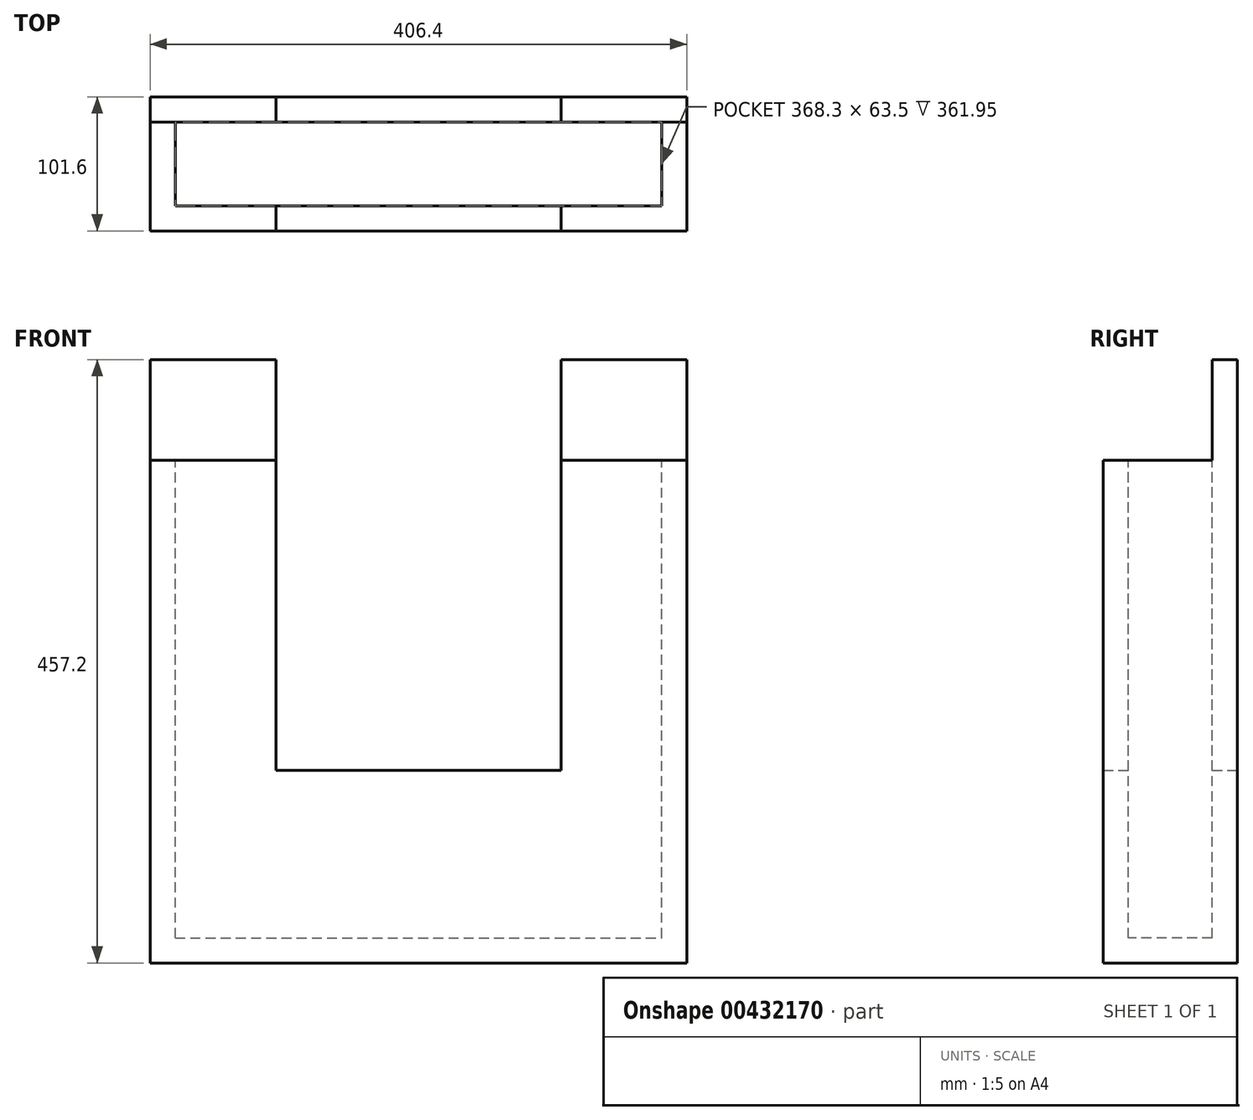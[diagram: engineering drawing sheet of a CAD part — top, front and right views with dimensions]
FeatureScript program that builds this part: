
annotation { "Feature Type Name" : "Feature", "Feature Type Description" : "" }
export const myFeature = defineFeature(function(context is Context, id is Id, definition is map)
    precondition{}
    {
        {
            var Q0;
            Q0=qCreatedBy(makeId("Front.planeOp"),FACE);
            var sketch = newSketch(context, id + "F0", { "sketchPlane" : qUnion([Q0])});
            skLineSegment(sketch, "E0.bottom", {"start": v(-199.76, 190.43) * mm, "end": v(206.64, 190.43) * mm});
            skLineSegment(sketch, "E0.top", {"start": v(-199.76, -266.77) * mm, "end": v(206.64, -266.77) * mm});
            skLineSegment(sketch, "E0.left", {"start": v(-199.76, 190.43) * mm, "end": v(-199.76, -266.77) * mm});
            skLineSegment(sketch, "E0.right", {"start": v(206.64, 190.43) * mm, "end": v(206.64, -266.77) * mm});
            skSolve(sketch);
        }
        {
            var Q0;
            Q0 = qSketchRegion(id + "F0", true);
            extrude(context, id + "F1", {"entities" : qUnion([Q0]), "depth" : 101.6 * mm});
        }
        {
            var Q0;
            Q0=makeQuery(id+"F1.opExtrude","SWEPT_FACE",FACE,{"disambiguationData":[OSD([sQuery(id+"F0.wireOp",EDGE,"E0.right")])]});
            var sketch = newSketch(context, id + "F2", { "sketchPlane" : qUnion([Q0])});
            skLineSegment(sketch, "E1.bottom", {"start": v(-101.6, 190.43) * mm, "end": v(-19.05, 190.43) * mm});
            skLineSegment(sketch, "E1.top", {"start": v(-101.6, 114.23) * mm, "end": v(-19.05, 114.23) * mm});
            skLineSegment(sketch, "E1.left", {"start": v(-101.6, 190.43) * mm, "end": v(-101.6, 114.23) * mm});
            skLineSegment(sketch, "E1.right", {"start": v(-19.05, 190.43) * mm, "end": v(-19.05, 114.23) * mm});
            skSolve(sketch);
        }
        {
            var Q0;
            Q0=makeQuery(id+"F2.imprint","IMPRINT",FACE,{"disambiguationData":[TD([[makeQuery(id+"F2.imprint","IMPRINT",EDGE,{"derivedFrom":sQuery(id+"F2.wireOp",EDGE,"E1.bottom")}),-1.0]])]});
            extrude(context, id + "F3", {"entities" : qUnion([Q0]), "operationType" : NewBodyOperationType.REMOVE, "oppositeDirection" : true, "depth" : 406.4 * mm});
        }
        {
            var Q0;
            Q0=makeQuery(id+"F3.boolean.opBoolean","COPY",FACE,{"derivedFrom":makeQuery(id+"F3.opExtrude","SWEPT_FACE",FACE,{"disambiguationData":[OSD([sQuery(id+"F2.wireOp",EDGE,"E1.top")])]})});
            var sketch = newSketch(context, id + "F4", { "sketchPlane" : qUnion([Q0])});
            skLineSegment(sketch, "E2.bottom", {"start": v(-180.7, -19.05) * mm, "end": v(187.6, -19.05) * mm});
            skLineSegment(sketch, "E2.top", {"start": v(-180.7, -82.55) * mm, "end": v(187.6, -82.55) * mm});
            skLineSegment(sketch, "E2.left", {"start": v(-180.7, -19.05) * mm, "end": v(-180.7, -82.55) * mm});
            skLineSegment(sketch, "E2.right", {"start": v(187.6, -19.05) * mm, "end": v(187.6, -82.55) * mm});
            skSolve(sketch);
        }
        {
            var Q0;
            Q0=makeQuery(id+"F4.imprint","IMPRINT",FACE,{"disambiguationData":[TD([[makeQuery(id+"F4.imprint","IMPRINT",EDGE,{"derivedFrom":sQuery(id+"F4.wireOp",EDGE,"E2.bottom")}),-1.0]])]});
            extrude(context, id + "F5", {"entities" : qUnion([Q0]), "operationType" : NewBodyOperationType.REMOVE, "oppositeDirection" : true, "depth" : 361.95 * mm});
        }
        {
            var Q0;
            Q0=makeQuery(id+"F1.opExtrude","CAP_FACE",FACE,{"disambiguationData":[OSD([sQuery(id+"F0.wireOp",EDGE,"E0.bottom"),sQuery(id+"F0.wireOp",EDGE,"E0.top"),sQuery(id+"F0.wireOp",EDGE,"E0.left"),sQuery(id+"F0.wireOp",EDGE,"E0.right")])],"isStart":true});
            var sketch = newSketch(context, id + "F6", { "sketchPlane" : qUnion([Q0])});
            skLineSegment(sketch, "E3.bottom", {"start": v(-111.4, 190.43) * mm, "end": v(104.5, 190.43) * mm});
            skLineSegment(sketch, "E3.top", {"start": v(-111.4, -120.72) * mm, "end": v(104.5, -120.72) * mm});
            skLineSegment(sketch, "E3.left", {"start": v(-111.4, 190.43) * mm, "end": v(-111.4, -120.72) * mm});
            skLineSegment(sketch, "E3.right", {"start": v(104.5, 190.43) * mm, "end": v(104.5, -120.72) * mm});
            skSolve(sketch);
        }
        {
            var Q0;
            Q0=makeQuery(id+"F6.imprint","IMPRINT",FACE,{"disambiguationData":[TD([[makeQuery(id+"F6.imprint","IMPRINT",EDGE,{"derivedFrom":sQuery(id+"F6.wireOp",EDGE,"E3.bottom")}),1.0]])]});
            extrude(context, id + "F7", {"entities" : qUnion([Q0]), "operationType" : NewBodyOperationType.REMOVE, "oppositeDirection" : true, "depth" : 101.6 * mm});
        }
    });
